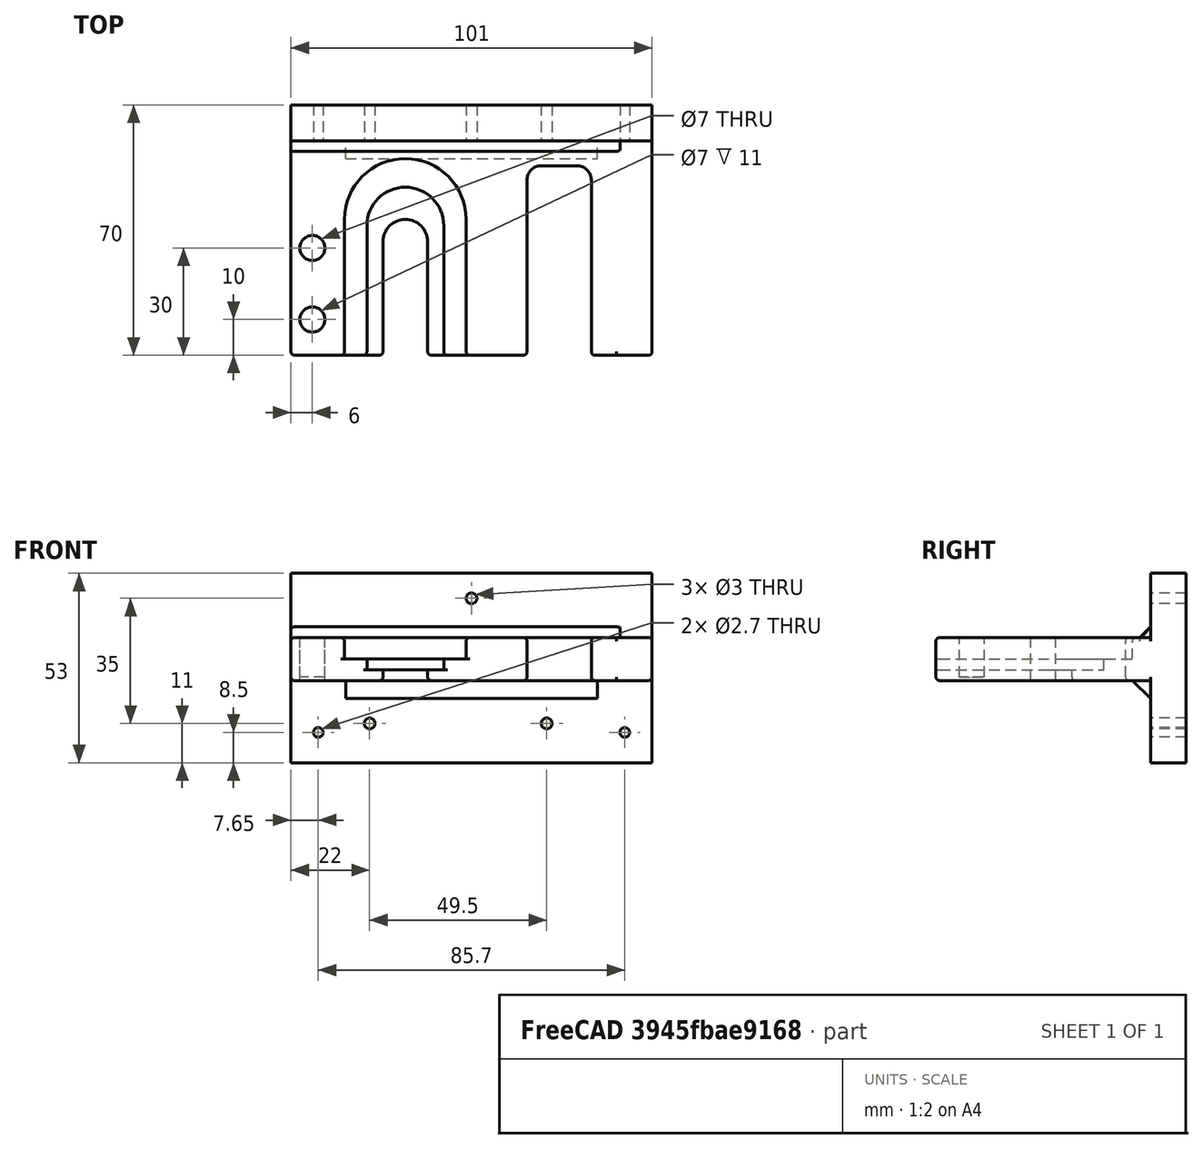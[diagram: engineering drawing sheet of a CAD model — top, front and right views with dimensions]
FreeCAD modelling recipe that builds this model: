
FCSTD DOCUMENT  (FreeCAD 0.19R24276 (Git))
Label: soporte_taladro_martillo
License: All rights reserved
LicenseURL: http://en.wikipedia.org/wiki/All_rights_reserved
objects: Part::Cut×17, Part::Cylinder×15, Part::Box×14, Part::MultiFuse×12, Part::Fillet×9, Part::Chamfer×1, Sketcher::SketchObject×1, PartDesign::Pad×1, PartDesign::Body×1, Mesh::Feature×1
note: 72 computed .brp shape members not serialized (recipe doc carries the construction recipe); baked Part::Feature solids carry a one-line shape summary decoded from their .brp

FEATURE [Part::Box] Box  label="Cube"
  AttacherType = Attacher::AttachEngine3D
  Height = 12
  Length = 40
  Width = 60
FEATURE [Part::Box] Box001  label="Cube001"
  AttacherType = Attacher::AttachEngine3D
  Height = 15
  Length = 12.5
  Placement = pos=(13.75,0,0) rot=(0,0,1;0rad)
  Width = 31.75
FEATURE [Part::Cylinder] Cylinder
  Angle = 360
  AttacherType = Attacher::AttachEngine3D
  Height = 15
  Placement = pos=(20,31.75,0) rot=(0,0,1;0rad)
  Radius = 6.25
FEATURE [Part::MultiFuse] Fusion
  Refine = true
  Shapes = -> [Box001,Cylinder]
FEATURE [Part::Cut] Cut
  Base = -> Box
  Refine = true
  Tool = -> Fusion
FEATURE [Part::Cylinder] Cylinder001
  Angle = 360
  AttacherType = Attacher::AttachEngine3D
  Height = 15
  Placement = pos=(20,36.25,3) rot=(0,0,1;0rad)
  Radius = 10.75
FEATURE [Part::Box] Box002  label="Cube002"
  AttacherType = Attacher::AttachEngine3D
  Height = 15
  Length = 21.5
  Placement = pos=(9.25,0,3) rot=(0,0,1;0rad)
  Width = 36.25
FEATURE [Part::MultiFuse] Fusion001
  Refine = true
  Shapes = -> [Cylinder001,Box002]
FEATURE [Part::Box] Box003  label="Cube003"
  AttacherType = Attacher::AttachEngine3D
  Height = 15
  Length = 34
  Placement = pos=(3,0,6) rot=(0,0,1;0rad)
  Width = 38
FEATURE [Part::Cut] Cut001
  Base = -> Cut
  Refine = true
  Tool = -> Fusion001
FEATURE [Part::Cylinder] Cylinder002
  Angle = 360
  AttacherType = Attacher::AttachEngine3D
  Height = 15
  Placement = pos=(20,38,6) rot=(0,0,1;0rad)
  Radius = 17
FEATURE [Part::MultiFuse] Fusion002
  Refine = true
  Shapes = -> [Box003,Cylinder002]
FEATURE [Part::Cut] Cut002
  Base = -> Cut001
  Refine = true
  Tool = -> Fusion002
FEATURE [Part::Box] Box004  label="Cube004"
  AttacherType = Attacher::AttachEngine3D
  Height = 12
  Length = 16
  Placement = pos=(39,0,0) rot=(0,0,1;0rad)
  Width = 60
FEATURE [Part::Box] Box005  label="Cube005"
  AttacherType = Attacher::AttachEngine3D
  Height = 12
  Length = 26
  Placement = pos=(54,0,0) rot=(0,0,1;0rad)
  Width = 60
FEATURE [Part::MultiFuse] Fusion003
  Refine = true
  Shapes = -> [Box004,Box005]
FEATURE [Part::MultiFuse] Fusion004
  Refine = true
  Shapes = -> [Cut002,Fusion003]
FEATURE [Part::Box] Box006  label="Cube006"
  AttacherType = Attacher::AttachEngine3D
  Height = 15
  Length = 18
  Placement = pos=(54,0,0) rot=(0,0,1;0rad)
  Width = 53
FEATURE [Part::Cut] Cut003
  Base = -> Fusion004
  Refine = true
  Tool = -> Box006
FEATURE [Part::Box] Box007  label="Cube007"
  AttacherType = Attacher::AttachEngine3D
  Height = 12
  Length = 12
  Placement = pos=(-12,0,0) rot=(0,0,1;0rad)
  Width = 60
FEATURE [Part::Cylinder] Cylinder003
  Angle = 360
  AttacherType = Attacher::AttachEngine3D
  Height = 15
  Placement = pos=(-6,30,0) rot=(0,0,1;0rad)
  Radius = 3.5
FEATURE [Part::Cylinder] Cylinder004
  Angle = 360
  AttacherType = Attacher::AttachEngine3D
  Height = 15
  Placement = pos=(-6,10,1) rot=(0,0,1;0rad)
  Radius = 3.5
FEATURE [Part::Fillet] Fillet
  Base = -> Cut003
  Edges = 2 edges r=4: [Edge29,Edge42]
FEATURE [Part::Fillet] Fillet001
  Base = -> Fillet
  Edges = 6 edges r=1: [Edge15,Edge20,Edge30,Edge34,Edge36,Edge38]
FEATURE [Part::Fillet] Fillet002
  Base = -> Box007
  Edges = 1 edges r=1: [Edge1]
FEATURE [Part::Fillet] Fillet003
  Base = -> Fillet001
  Edges = 3 edges r=1: [Edge53,Edge55,Edge57]
FEATURE [Part::Cut] Cut004
  Base = -> Fillet002
  Refine = true
  Tool = -> Cylinder004
FEATURE [Part::Cut] Cut005
  Base = -> Cut004
  Refine = true
  Tool = -> Cylinder003
FEATURE [Part::MultiFuse] Fusion005
  Refine = true
  Shapes = -> [Cut005,Fillet003]
FEATURE [Part::Fillet] Fillet004
  Base = -> Fusion005
  Edges = 6 edges r=1: [Edge8,Edge14,Edge22,Edge50,Edge69,Edge102]
FEATURE [Part::Box] Box008  label="Cube008"
  AttacherType = Attacher::AttachEngine3D
  Height = 30
  Length = 92
  Placement = pos=(-12,60,0) rot=(0,0,1;0rad)
  Width = 10
FEATURE [Part::MultiFuse] Fusion006
  Refine = true
  Shapes = -> [Fillet004,Box008]
FEATURE [Part::Chamfer] Chamfer
  Base = -> Fusion006
  Edges = 1 edges r=3: [Edge51]
FEATURE [Part::Fillet] Fillet005
  Base = -> Chamfer
  Edges = 1 edges r=1: [Edge25]
FEATURE [Part::Box] Box009  label="Cube009"
  AttacherType = Attacher::AttachEngine3D
  Height = 30
  Length = 92
  Placement = pos=(-12,60,-19) rot=(0,0,1;0rad)
  Width = 10
FEATURE [Part::MultiFuse] Fusion007
  Refine = true
  Shapes = -> [Fillet005,Box009]
FEATURE [Part::Box] Box010  label="Cube010"
  AttacherType = Attacher::AttachEngine3D
  Height = 8
  Length = 86
  Placement = pos=(-9,60,-5) rot=(1,0,0;0.785398rad)
  Width = 8
FEATURE [Part::MultiFuse] Fusion008
  Refine = true
  Shapes = -> [Fusion007,Box010]
FEATURE [Part::Cylinder] Cylinder005
  Angle = 360
  AttacherType = Attacher::AttachEngine3D
  Height = 20
  Placement = pos=(10,74,-12) rot=(1,0,0;1.5708rad)
  Radius = 1.5
FEATURE [Part::Cylinder] Cylinder006
  Angle = 360
  AttacherType = Attacher::AttachEngine3D
  Height = 20
  Placement = pos=(59.5,74,-12) rot=(1,0,0;1.5708rad)
  Radius = 1.5
FEATURE [Part::Cylinder] Cylinder007
  Angle = 360
  AttacherType = Attacher::AttachEngine3D
  Height = 20
  Placement = pos=(34,74,23) rot=(1,0,0;1.5708rad)
  Radius = 1.5
FEATURE [Part::Cut] Cut006
  Base = -> Fusion008
  Refine = true
  Tool = -> Cylinder005
FEATURE [Part::Cut] Cut007
  Base = -> Cut006
  Refine = true
  Tool = -> Cylinder007
FEATURE [Part::Cut] Cut008
  Base = -> Cut007
  Refine = true
  Tool = -> Cylinder006
FEATURE [Part::Cylinder] Cylinder008
  Angle = 360
  AttacherType = Attacher::AttachEngine3D
  Height = 40
  Placement = pos=(34,86,23) rot=(1,0,0;1.5708rad)
  Radius = 1.5
FEATURE [Part::Cut] Cut009
  Base = -> Cut008
  Refine = true
  Tool = -> Cylinder008
FEATURE [Part::Box] Box011  label="Cube011"
  AttacherType = Attacher::AttachEngine3D
  Height = 20.7
  Length = 15.3
  Placement = pos=(-12,39.3,-20.7) rot=(0,0,1;0rad)
  Width = 20.7
FEATURE [Part::Box] Box012  label="Cube012"
  AttacherType = Attacher::AttachEngine3D
  Height = 20.7
  Length = 15.3
  Placement = pos=(73.7,39.3,-20.7) rot=(0,0,1;0rad)
  Width = 20.7
FEATURE [Part::Box] Box013  label="Cube013"
  AttacherType = Attacher::AttachEngine3D
  Height = 30
  Length = 92
  Placement = pos=(-12,60,-23) rot=(0,0,1;0rad)
  Width = 10
FEATURE [Part::MultiFuse] Fusion009
  Refine = true
  Shapes = -> [Box013,Cut009]
FEATURE [Sketcher::SketchObject] Sketch
  FullyConstrained = true
  MapMode = 5
  Placement = pos=(0,0,0) rot=(0.57735,0.57735,0.57735;2.0944rad)
  Support = -> [YZ_Plane]
  sketch-geometry (8):
    g0: LineSegment StartX=0 StartY=0 StartZ=0 EndX=0 EndY=12 EndZ=0
    g1: LineSegment StartX=0 StartY=12 StartZ=0 EndX=60 EndY=12 EndZ=0
    g2: LineSegment StartX=60 StartY=12 StartZ=0 EndX=60 EndY=30 EndZ=0
    g3: LineSegment StartX=60 StartY=30 StartZ=0 EndX=70 EndY=30 EndZ=0
    g4: LineSegment StartX=70 StartY=30 StartZ=0 EndX=70 EndY=-23 EndZ=0
    g5: LineSegment StartX=70 StartY=-23 StartZ=0 EndX=60 EndY=-23 EndZ=0
    g6: LineSegment StartX=60 StartY=-23 StartZ=0 EndX=60 EndY=0 EndZ=0
    g7: LineSegment StartX=60 StartY=0 StartZ=0 EndX=0 EndY=0 EndZ=0
  constraints (23):
    c: Coincident(g-1,g0)
    c: PointOnObject(g0,g-2)
    c: Coincident(g0,g1)
    c: Horizontal(g1)
    c: Coincident(g1,g2)
    c: Vertical(g2)
    c: Coincident(g2,g3)
    c: Horizontal(g3)
    c: Coincident(g3,g4)
    c: Vertical(g4)
    c: Coincident(g4,g5)
    c: Horizontal(g5)
    c: Coincident(g5,g6)
    c: PointOnObject(g6,g-1)
    c: Vertical(g6)
    c: Coincident(g6,g7)
    c: Coincident(g7,g0)
    c: DistanceY(g0,g0) = 12
    c: DistanceX(g1,g1) = 60
    c: DistanceY(g2,g2) = 18
    c: DistanceX(g3,g3) = 10
    c: DistanceY(g4,g4) = 53
    c: DistanceX(g5,g5) = 10
FEATURE [PartDesign::Pad] Pad
  Direction = (1,1,1)
  Length = 10
  Length2 = 100
  Placement = pos=(0,0,0) rot=(0.57735,0.57735,0.57735;2.0944rad)
  Profile = -> Sketch
  Refine = true
  Type = 0
FEATURE [PartDesign::Body] Body
  Group = -> [Sketch,Pad]
  Origin = -> Origin
  Placement = pos=(79,0,0) rot=(0,0,1;0rad)
  Tip = -> Pad
FEATURE [Part::MultiFuse] Fusion010
  Refine = true
  Shapes = -> [Body,Fusion009]
FEATURE [Part::Fillet] Fillet006
  Base = -> Fusion010
  Edges = 1 edges r=1: [Edge2]
FEATURE [Part::Fillet] Fillet007
  Base = -> Fillet006
  Edges = 1 edges r=1: [Edge17]
FEATURE [Part::Fillet] Fillet008
  Base = -> Fillet007
  Edges = 1 edges r=1: [Edge9]
FEATURE [Part::Cut] Cut010
  Base = -> Fillet008
  Refine = true
  Tool = -> Box012
FEATURE [Part::Cut] Cut011
  Base = -> Cut010
  Refine = true
  Tool = -> Box011
FEATURE [Part::Cylinder] Cylinder009
  Angle = 360
  AttacherType = Attacher::AttachEngine3D
  Height = 20
  Placement = pos=(10,74,-12) rot=(1,0,0;1.5708rad)
  Radius = 1.5
FEATURE [Part::Cylinder] Cylinder010
  Angle = 360
  AttacherType = Attacher::AttachEngine3D
  Height = 10
  Placement = pos=(34,70,23) rot=(1,0,0;1.5708rad)
  Radius = 1.5
FEATURE [Part::Cylinder] Cylinder011
  Angle = 360
  AttacherType = Attacher::AttachEngine3D
  Height = 20
  Placement = pos=(59.5,74,-12) rot=(1,0,0;1.5708rad)
  Radius = 1.5
FEATURE [Part::Cut] Cut012
  Base = -> Cut011
  Refine = true
  Tool = -> Cylinder009
FEATURE [Part::Cut] Cut013
  Base = -> Cut012
  Refine = true
  Tool = -> Cylinder011
FEATURE [Part::Cylinder] Cylinder012
  Angle = 360
  AttacherType = Attacher::AttachEngine3D
  Height = 20
  Placement = pos=(38.5,74,23) rot=(1,0,0;1.5708rad)
  Radius = 1.5
FEATURE [Part::Cut] Cut014
  Base = -> Cut013
  Refine = true
  Tool = -> Cylinder012
FEATURE [Part::MultiFuse] Fusion011
  Refine = true
  Shapes = -> [Cut014,Cylinder010]
FEATURE [Part::Cylinder] Cylinder013
  Angle = 360
  AttacherType = Attacher::AttachEngine3D
  Height = 20
  Placement = pos=(-4.35,76,-14.5) rot=(1,0,0;1.5708rad)
  Radius = 1.35
FEATURE [Part::Cylinder] Cylinder014
  Angle = 360
  AttacherType = Attacher::AttachEngine3D
  Height = 20
  Placement = pos=(81.35,76,-14.5) rot=(1,0,0;1.5708rad)
  Radius = 1.35
FEATURE [Part::Cut] Cut015
  Base = -> Fusion011
  Refine = true
  Tool = -> Cylinder014
FEATURE [Part::Cut] Cut016
  Base = -> Cut015
  Refine = true
  Tool = -> Cylinder013
FEATURE [Mesh::Feature] Mesh  label="Cut016 (Meshed)"
